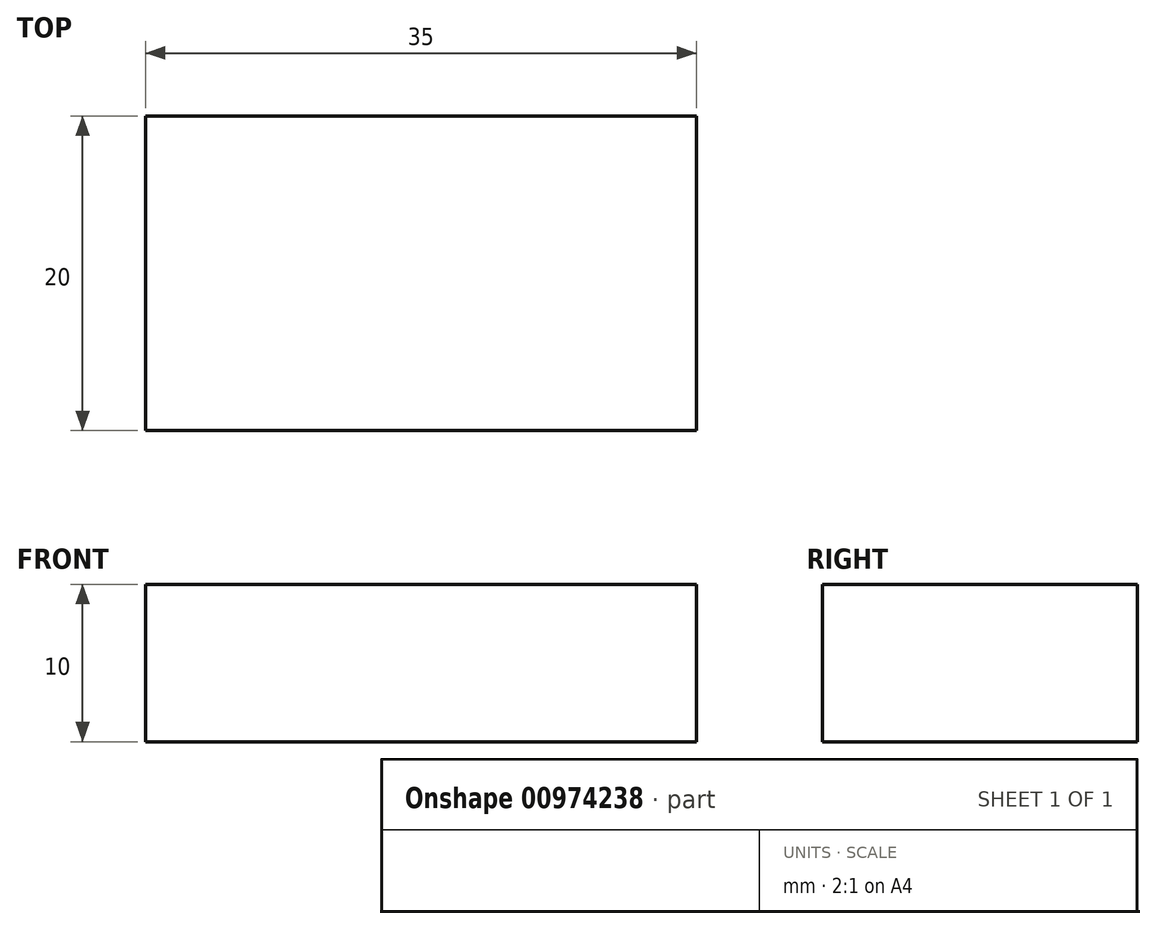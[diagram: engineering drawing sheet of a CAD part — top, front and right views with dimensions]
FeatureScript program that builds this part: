
annotation { "Feature Type Name" : "Feature", "Feature Type Description" : "" }
export const myFeature = defineFeature(function(context is Context, id is Id, definition is map)
    precondition{}
    {
        {
            var Q0;
            Q0=qCreatedBy(makeId("Top.planeOp"),FACE);
            var sketch = newSketch(context, id + "F0", { "sketchPlane" : qUnion([Q0])});
            skLineSegment(sketch, "E0.bottom", {"start": v(0, 20) * mm, "end": v(35, 20) * mm});
            skLineSegment(sketch, "E0.top", {"start": v(0, 0) * mm, "end": v(35, 0) * mm});
            skLineSegment(sketch, "E0.left", {"start": v(0, 20) * mm, "end": v(0, 0) * mm});
            skLineSegment(sketch, "E0.right", {"start": v(35, 20) * mm, "end": v(35, 0) * mm});
            skSolve(sketch);
        }
        {
            var Q0;
            Q0 = qSketchRegion(id + "F0", true);
            extrude(context, id + "F1", {"entities" : qUnion([Q0]), "depth" : 10 * mm, "offsetDistance" : 25 * mm});
        }
    });
